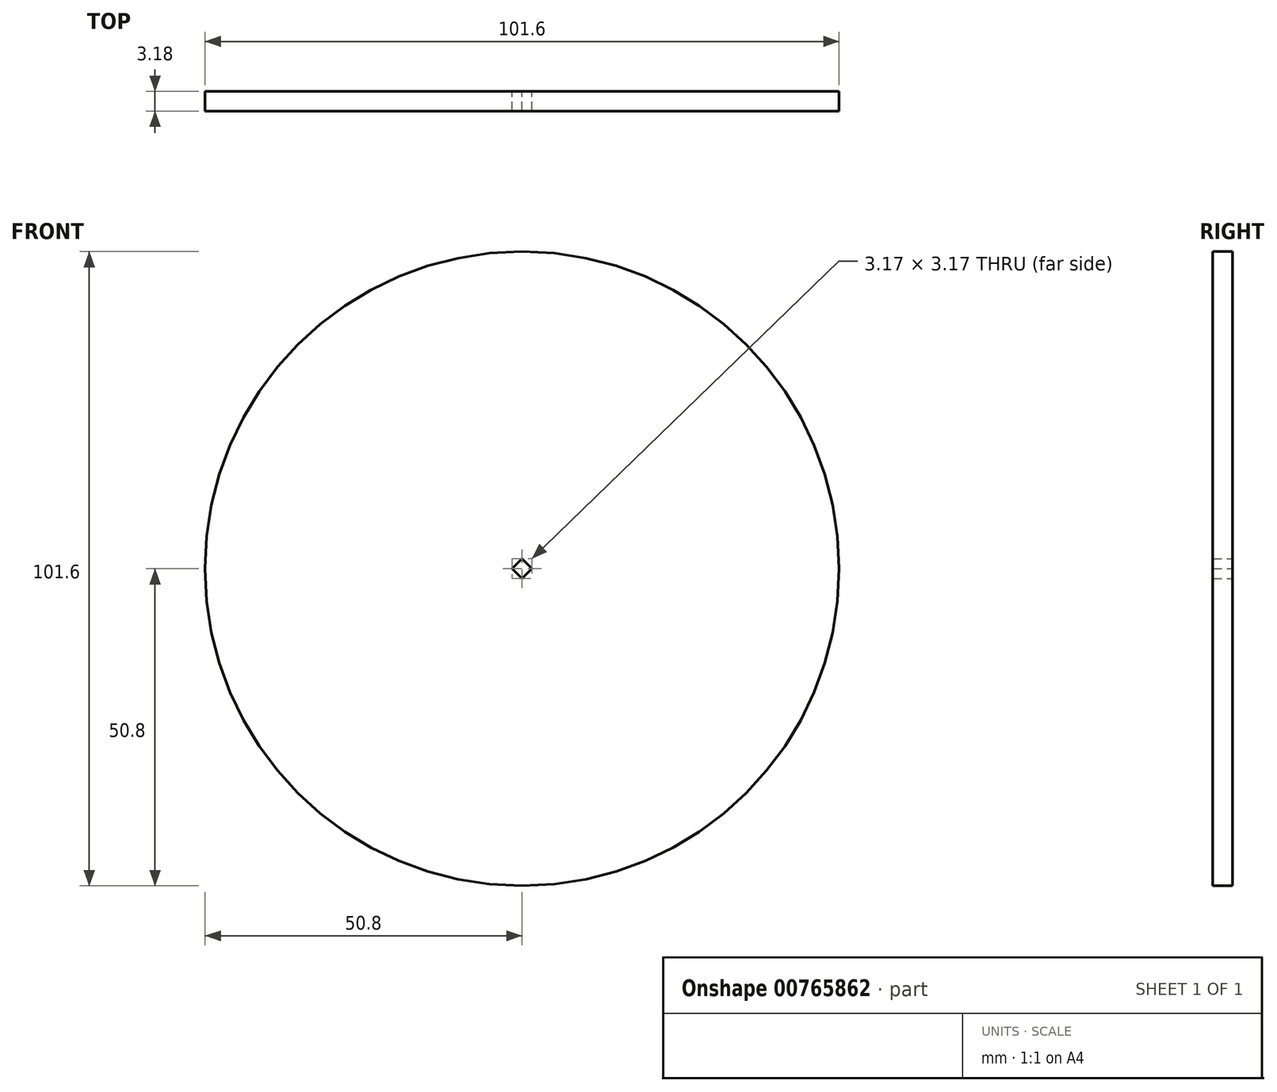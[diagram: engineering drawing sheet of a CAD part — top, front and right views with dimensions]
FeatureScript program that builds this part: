
annotation { "Feature Type Name" : "Feature", "Feature Type Description" : "" }
export const myFeature = defineFeature(function(context is Context, id is Id, definition is map)
    precondition{}
    {
        {
            var Q0;
            Q0=qCreatedBy(makeId("Front.planeOp"),FACE);
            var sketch = newSketch(context, id + "F0", { "sketchPlane" : qUnion([Q0])});
            skCircle(sketch, "E0", {"center": v(0, 0) * mm, "radius": 50.8 * mm});
            skLineSegment(sketch, "E1", {"start": v(0, 1.59) * mm, "end": v(-1.59, 0) * mm});
            skLineSegment(sketch, "E2", {"start": v(-1.59, 0) * mm, "end": v(0, -1.59) * mm});
            skLineSegment(sketch, "E3", {"start": v(0, -1.59) * mm, "end": v(1.59, 0) * mm});
            skLineSegment(sketch, "E4", {"start": v(1.59, 0) * mm, "end": v(0, 1.59) * mm});
            skSolve(sketch);
        }
        {
            var Q0;
            Q0=makeQuery(id+"F0.imprint","IMPRINT",FACE,{"disambiguationData":[TD([[makeQuery(id+"F0.imprint","IMPRINT",EDGE,{"derivedFrom":sQuery(id+"F0.wireOp",EDGE,"E0")}),1.0]])]});
            extrude(context, id + "F1", {"entities" : qUnion([Q0]), "depth" : 3.17 * mm, "offsetDistance" : 25.4 * mm});
        }
    });
